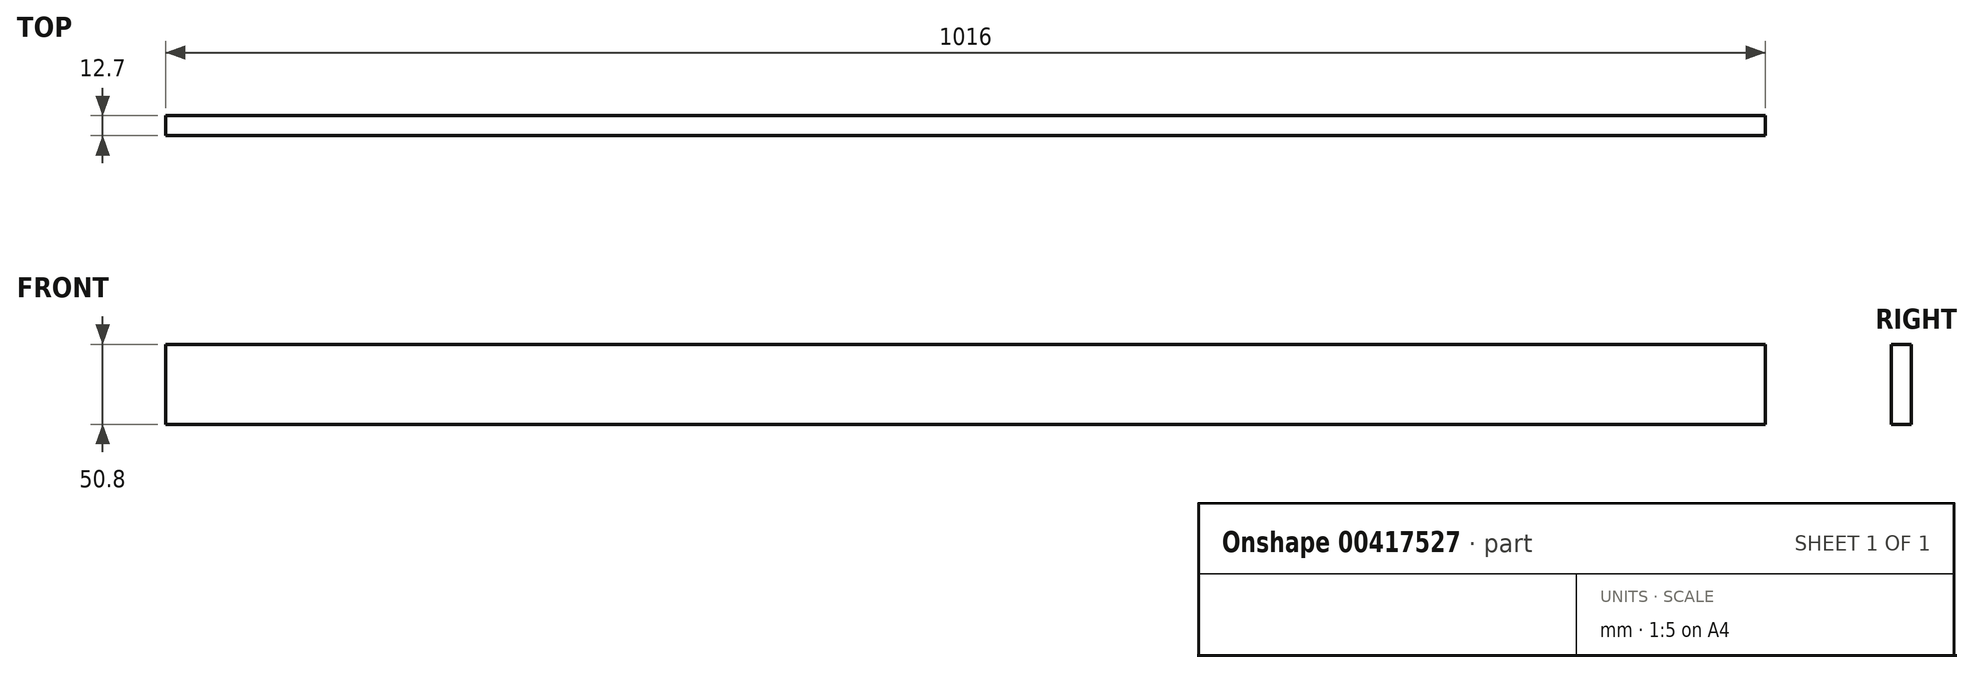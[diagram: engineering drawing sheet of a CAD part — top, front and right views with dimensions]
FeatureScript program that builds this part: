
annotation { "Feature Type Name" : "Feature", "Feature Type Description" : "" }
export const myFeature = defineFeature(function(context is Context, id is Id, definition is map)
    precondition{}
    {
        {
            var Q0;
            Q0=qCreatedBy(makeId("Front.planeOp"),FACE);
            var sketch = newSketch(context, id + "F0", { "sketchPlane" : qUnion([Q0])});
            skLineSegment(sketch, "E0.bottom", {"start": v(-508, 25.4) * mm, "end": v(508, 25.4) * mm});
            skLineSegment(sketch, "E0.top", {"start": v(-508, -25.4) * mm, "end": v(508, -25.4) * mm});
            skLineSegment(sketch, "E0.left", {"start": v(-508, 25.4) * mm, "end": v(-508, -25.4) * mm});
            skLineSegment(sketch, "E0.right", {"start": v(508, 25.4) * mm, "end": v(508, -25.4) * mm});
            skPoint(sketch, "E0.middle", {"position": v(0, 0) * mm});
            skSolve(sketch);
        }
        {
            var Q0;
            Q0 = qSketchRegion(id + "F0", true);
            extrude(context, id + "F1", {"entities" : qUnion([Q0]), "depth" : 12.7 * mm});
        }
    });
